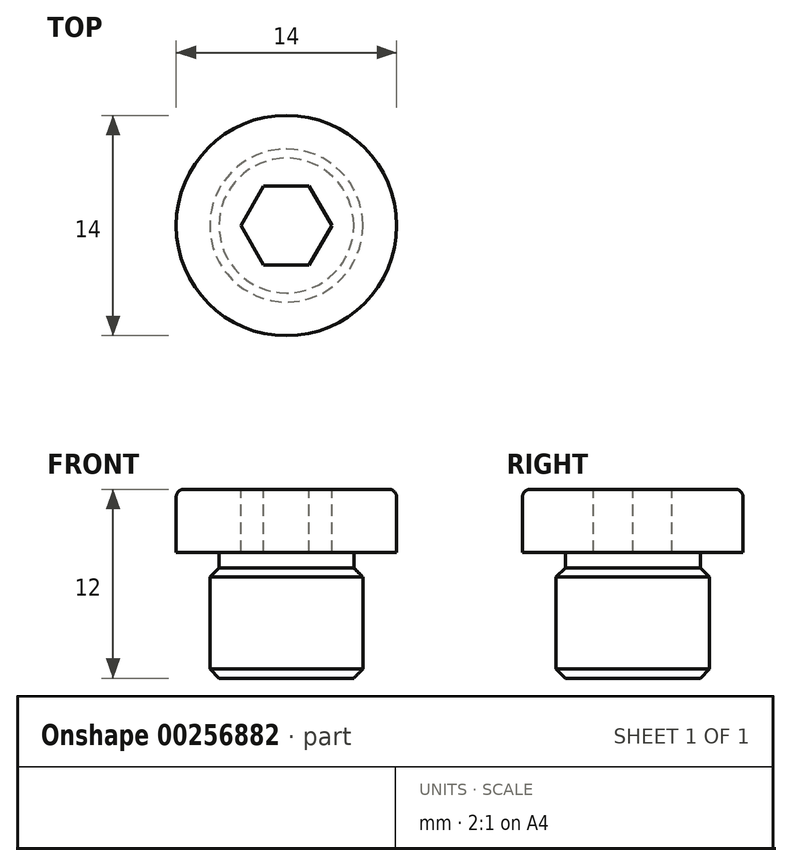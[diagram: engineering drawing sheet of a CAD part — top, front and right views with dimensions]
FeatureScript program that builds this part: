
annotation { "Feature Type Name" : "Feature", "Feature Type Description" : "" }
export const myFeature = defineFeature(function(context is Context, id is Id, definition is map)
    precondition{}
    {
        {
            var Q0;
            Q0=qCreatedBy(makeId("Front.planeOp"),FACE);
            var sketch = newSketch(context, id + "F0", { "sketchPlane" : qUnion([Q0])});
            skLineSegment(sketch, "E0", {"start": v(0, 0) * mm, "end": v(4.28, 0) * mm});
            skLineSegment(sketch, "E1", {"start": v(4.28, 0) * mm, "end": v(4.86, 0.58) * mm});
            skLineSegment(sketch, "E2", {"start": v(4.86, 0.58) * mm, "end": v(4.86, 6.42) * mm});
            skLineSegment(sketch, "E3", {"start": v(4.86, 6.42) * mm, "end": v(4.28, 7) * mm});
            skLineSegment(sketch, "E4", {"start": v(4.28, 7) * mm, "end": v(4.28, 8) * mm});
            skLineSegment(sketch, "E5", {"start": v(4.28, 8) * mm, "end": v(7, 8) * mm});
            skLineSegment(sketch, "E6", {"start": v(7, 8) * mm, "end": v(7, 11.5) * mm});
            skLineSegment(sketch, "E7", {"start": v(6.5, 12) * mm, "end": v(0, 12) * mm});
            skLineSegment(sketch, "E8", {"start": v(0, 12) * mm, "end": v(0, 0) * mm});
            skPoint(sketch, "E9.visualSharp", {"position": v(7, 12) * mm});
            skArc(sketch, "E9.filletArc", {"start": v(7, 11.5) * mm, "mid": v(6.85, 11.85) * mm, "end": v(6.5, 12) * mm});
            skSolve(sketch);
        }
        {
            var Q0;
            Q0=qSketchRegion(id+"F0",true);
            var Q1;
            Q1=sQuery(id+"F0.wireOp",EDGE,"E8");
            revolve(context, id + "F1", {"entities" : qUnion([Q0]), "axis" : qUnion([Q1]), "revolveType" : RevolveType.FULL});
        }
        {
            var Q0;
            Q0=makeQuery(id+"F1.opRevolve","SWEPT_FACE",FACE,{"disambiguationData":[OSD([sQuery(id+"F0.wireOp",EDGE,"E7")])]});
            var sketch = newSketch(context, id + "F2", { "sketchPlane" : qUnion([Q0])});
            skCircle(sketch, "E10.cCircle", {"center": v(0, 0) * mm, "radius": 2.5 * mm, "construction": true});
            skLineSegment(sketch, "E10.0", {"start": v(1.44, 2.5) * mm, "end": v(2.89, 0) * mm});
            skLineSegment(sketch, "E10.1", {"start": v(2.89, 0) * mm, "end": v(1.44, -2.5) * mm});
            skLineSegment(sketch, "E10.2", {"start": v(1.44, -2.5) * mm, "end": v(-1.44, -2.5) * mm});
            skLineSegment(sketch, "E10.3", {"start": v(-1.44, -2.5) * mm, "end": v(-2.89, 0) * mm});
            skLineSegment(sketch, "E10.4", {"start": v(-2.89, 0) * mm, "end": v(-1.44, 2.5) * mm});
            skLineSegment(sketch, "E10.5", {"start": v(-1.44, 2.5) * mm, "end": v(1.44, 2.5) * mm});
            skPoint(sketch, "E10.0.midPoint", {"position": v(2.17, 1.25) * mm});
            skSolve(sketch);
        }
        {
            var Q0;
            Q0=qSketchRegion(id+"F2",true);
            extrude(context, id + "F3", {"entities" : qUnion([Q0]), "operationType" : NewBodyOperationType.REMOVE, "oppositeDirection" : true, "depth" : 4 * mm});
        }
    });
